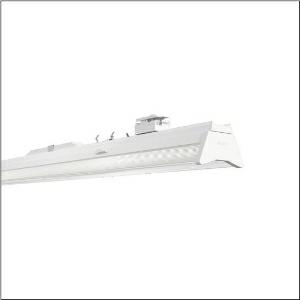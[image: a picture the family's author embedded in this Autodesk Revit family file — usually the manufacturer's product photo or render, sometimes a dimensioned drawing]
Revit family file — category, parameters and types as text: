
# Revit family: licross_r__21_performance_ho_52td16dn4e5m_0710
name_source: partatom
category: Lighting Fixtures
units: mm (PartAtom-declared; Revit-internal decimal feet)

## family parameters
Cut with Voids When Loaded = No
Host = Face
Light Source = No
Part Type = Normal
Room Calculation Point = No
Round Connector Dimension = Use Diameter
Shared = No

## types (1)
- --- (1 x LED, 14870 lm, 84.9 W, 4000K)
    Apparent Load = 85 VA
    CIE Flux Codes = 63 87 95 78 100
    Color Rendering = 80
    Color Temperature = 4000K
    Default Elevation = 1800 mm
    Description = Licross® 21 Performance HO, luminaire insert, of sheet steel, galvanised, coil coated, white, length: 1.500mm, width: 120mm, height: 123mm, LED rated luminous flux: 14.870lm, light colour: 840, control gear: DALI 2, with plug, 5-pole, with phase selection, mains connection: 220..240V, AC, 50/60Hz, rated input power: 85W, internal wiring halogen-free, primary light control with lens, of plastic, primary optical cover: cover, of PMMA, light emission: direct/indirect distribution, primary light characteristic: symmetric, protection rating (complete): IP54, insulation class (complete): insulation class I (protective earthing), certification: CE, ENEC, VDE, UKCA, protection symbol: D if used in an environment with non-conductive dust loads with corresponding accessories, impact resistance: IK06, permissible ambient temperature for indoor applications: -25..+35°C, corresponds to IFS (International Featured Standards) requirements for safety and quality in the food industry, reducing of maximum allowable ambient temperature of 5°C with ceiling mounting, LABS conformity tested according to VDMA 24364:2018-05, packaging unit: 1 piece
    Height = 114 mm
    Lamp = 1 x LED
    Lamp Light Flux = 14870 lm
    Lamp Power = 84.9 W
    Lamp count = 1
    Length = 1500 mm
    Luminous efficacy = 175 lm/W
    Manufacturer = Siteco
    ModVariant = No
    Model = 52TD16DN4E5M
    Mounting Place = Ceiling
    Mounting Type = Pendant
    Number of Poles = 1
    OnlyDefault = Yes
    Power Factor = 1
    Product Name = Licross® 21 Performance HO
    Product group = luminaire insert | ceiling pendant
    ProductGroupID = 902
    Protection Class = Protection class I
    Protection Degree = IP 54
    RLX_Detail_Level = 1
    RLX_Emergency_Light_Flux = 0 lm
    RLX_Emergency_Type = 0
    RLX_Emergency_Type_DB = No
    RlxData = <blob elided: 34117 chars, md5=f9b16d9b>
    Socket = socket
    Standby Power = 0 W
    System Light Flux = 14870 lm
    System Power = 85 W
    Type Comments = factory setting: luminous flux: 100 % | dim-lin: 254 | 484 mA
    Type Image = l_1256138.jpg
    URL = http://relux.com
    VarID = @adj_150827
    Voltage = 0 V
    Weight = 0.00 kg
    Width = 120 mm

## geometry (parser evidence)
native form markers: Blend x4, Sweep x11
no freeform markers — native parametric forms only
